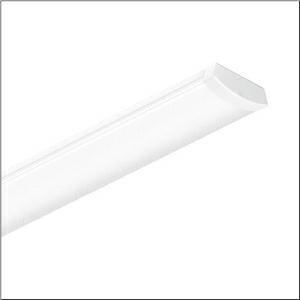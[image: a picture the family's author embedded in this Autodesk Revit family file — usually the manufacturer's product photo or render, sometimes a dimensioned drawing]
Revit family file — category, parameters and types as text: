
# Revit family: siluette_r__21_51ln12mnm70a3g_252a
name_source: partatom
category: Lighting Fixtures
units: mm (PartAtom-declared; Revit-internal decimal feet)

## family parameters
Cut with Voids When Loaded = No
Host = Face
Light Source = No
Part Type = Normal
Room Calculation Point = No
Round Connector Dimension = Use Diameter
Shared = No

## types (1)
- --- (1 x LED, 4320 lm, 28.8 W, 5000K)
    Apparent Load = 29 VA
    CIE Flux Codes = 43 73 92 94 100
    Color Rendering = 80
    Color Temperature = 5000K
    Default Elevation = 1800 mm
    Description = Siluette® 21, office luminaire, primary optical cover: enclosure, of PC, frosted, light emission: direct distribution, primary light characteristic: symmetric, installation type: suspended mounting, surface-mounted, LED, rated luminous flux: 7.150lm, luminous efficacy: 142lm/W, light colour: 830/840/850, colour temperature: 3000/4000/5000K, control gear: ON/OFF Multilumen, with terminal, 4-pole, mains connection: 220..240V, AC, 50/60Hz, rated input power: 51W, control gear: single battery element, housing, of sheet steel, white, length: 1.500mm, width: 152mm, height: 53mm, end cap, of PMMA, white, protection rating (complete): IP44, insulation class (complete): insulation class I (protective earthing), certification: CE, UKCA, protection symbol: D, impact resistance: IK04, permissible operating ambient temperature: +5..+40°C, standard: EN 60598-2-22, corresponds to IFS (International Featured Standards) requirements for safety and quality in the food industry, contact your sales advisor before using the luminaires in applications with unclear chemical exposure, large temperature fluctuations or condensation-forming humidity, packaging unit: 1 piece
    Height = 52 mm  [stored 0.170604 ft]
    Lamp = 1 x LED
    Lamp Light Flux = 4320 lm
    Lamp Power = 28.8 W
    Lamp count = 1
    Length = 1485 mm
    Luminous efficacy = 150 lm/W
    Manufacturer = Siteco
    ModVariant = No
    Model = 51LN12MNM70A3G
    Mounting Place = Ceiling
    Mounting Type = Pendant
    Number of Poles = 1
    OnlyDefault = Yes
    Power Factor = 1
    Product Name = Siluette® 21
    Product group = office luminaire | ceiling pendant
    ProductGroupID = 903
    Protection Class = Protection class I
    Protection Degree = IP 44
    RLX_Detail_Level = 1
    RLX_Emergency_Light_Flux = 0 lm
    RLX_Emergency_Type = 0
    RLX_Emergency_Type_DB = No
    RlxData = <blob elided: 19537 chars, md5=43b3e754>
    Socket = socket
    Standby Power = 0 W
    System Light Flux = 4320 lm
    System Power = 29 W
    Type Comments = individual setting: colour temperature 5000K, luminous flux: 61 % | (OFF | OFF | ON) | 200 mA
    Type Image = l_1296910.jpg
    URL = http://relux.com
    VarID = @adj_079477
    Voltage = 0 V
    Weight = 0.00 kg
    Width = 152 mm

note: [stored X ft] marks values corroborated as IEEE doubles in the binary element streams (Revit-internal decimal feet)

## geometry (parser evidence)
native form markers: Blend x4, Sweep x13
no freeform markers — native parametric forms only
